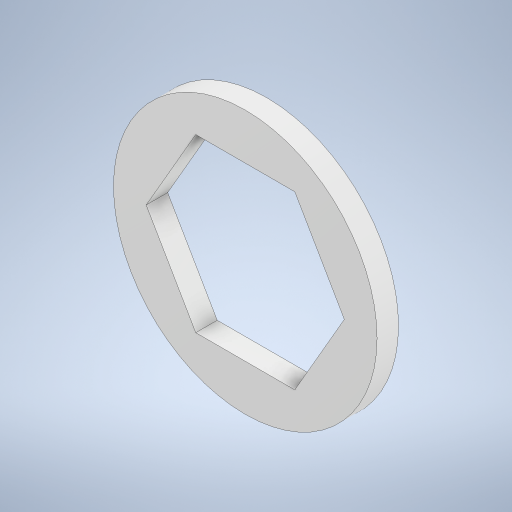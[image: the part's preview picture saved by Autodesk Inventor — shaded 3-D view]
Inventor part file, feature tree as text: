
AUTODESK INVENTOR PART (.ipt)
format: ipt  version: 2024 (Build 280153000, 153)  size: 238,080 bytes
history: native  units: in
note: dims shown in document units (in); Inventor stores cm internally (conversion verified against a paired STEP export)
features: extrude x1, sketch x1
ambient origin geometry x8: Origin, YZ Plane, XZ Plane, XY Plane, X Axis, Y Axis, Z Axis, Center Point
bodies: Solid1 (feature_tree)
feature tree (2):
  extrude  "Extrusion1"  Depth=0.5in
  sketch  "Sketch1"  dims[d0=0.768in d1=0.5in d2=0.0625in d3=0.0in]
